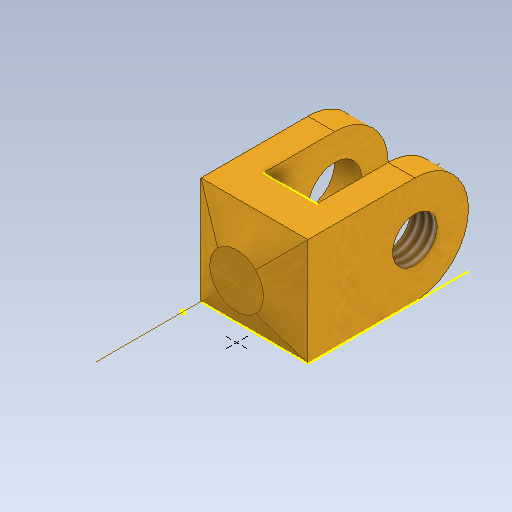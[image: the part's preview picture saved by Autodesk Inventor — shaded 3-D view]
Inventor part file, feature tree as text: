
AUTODESK INVENTOR PART (.ipt)
format: ipt  version: 2020 (Build 240168000, 168)  size: 193,536 bytes
history: native  units: mm
features: sketch x8, extrude x2, hole x2, other x2, plane x1, loft x1, thread x1, fillet x1, projected_geometry x1
ambient origin geometry x8: Origin, YZ Plane, XZ Plane, XY Plane, X Axis, Y Axis, Z Axis, Center Point
bodies: Solid1 (feature_tree)
feature tree (19):
  extrude  "Extrusion1"  Depth=9.0mm
  sketch  "Sketch2"  dims[d2=6.0mm d3=0.0mm d4=3.0mm]
  sketch  "Sketch3"  dims[d5=1.5mm d6=3.0mm]
  plane  "Work Plane1"
  sketch  "Sketch4"  dims[d7=1.0mm d8=3.0mm]
  loft  "Loft1"
  extrude  "Extrusion2"  Depth=3.0mm
  hole  "Hole1"  [1 undecoded]
  hole  "Hole2"  [1 undecoded]
  thread  "Thread1"  [1 undecoded]
  fillet  "Fillet1"  Radius=6.0mm
  sketch  "Sketch8"  dims[d24=3.0mm d25=6.0mm d26=4.0mm d27=2.0mm d28=90.0deg d29=1.5mm d30=20.594885mm d31=1.5mm d32=0.0mm d33=3.0mm]
  other  "Work Axis1"
  sketch  "Sketch1"  dims[d0=6.0mm d1=9.0mm]
  sketch  "Sketch5"  dims[d9=0.0mm d10=90.0deg d11=0.0mm d12=90.0deg d13=7.0mm d14=0.0mm d15=6.0mm]
  other  "Edges1"
  sketch  "Sketch6"  dims[d16=3.0mm]
  sketch  "Sketch7"  dims[d17=2.5mm d18=6.0mm d19=4.0mm d20=2.0mm d21=90.0deg d22=1.5mm d23=20.594885mm]
  projected_geometry  "Projected Loop1"
note: 3 required parameter values undecoded (feature->parameter linkage not recoverable at this tier; creation-order binding heuristic only, values carry confidence <= 0.55)
